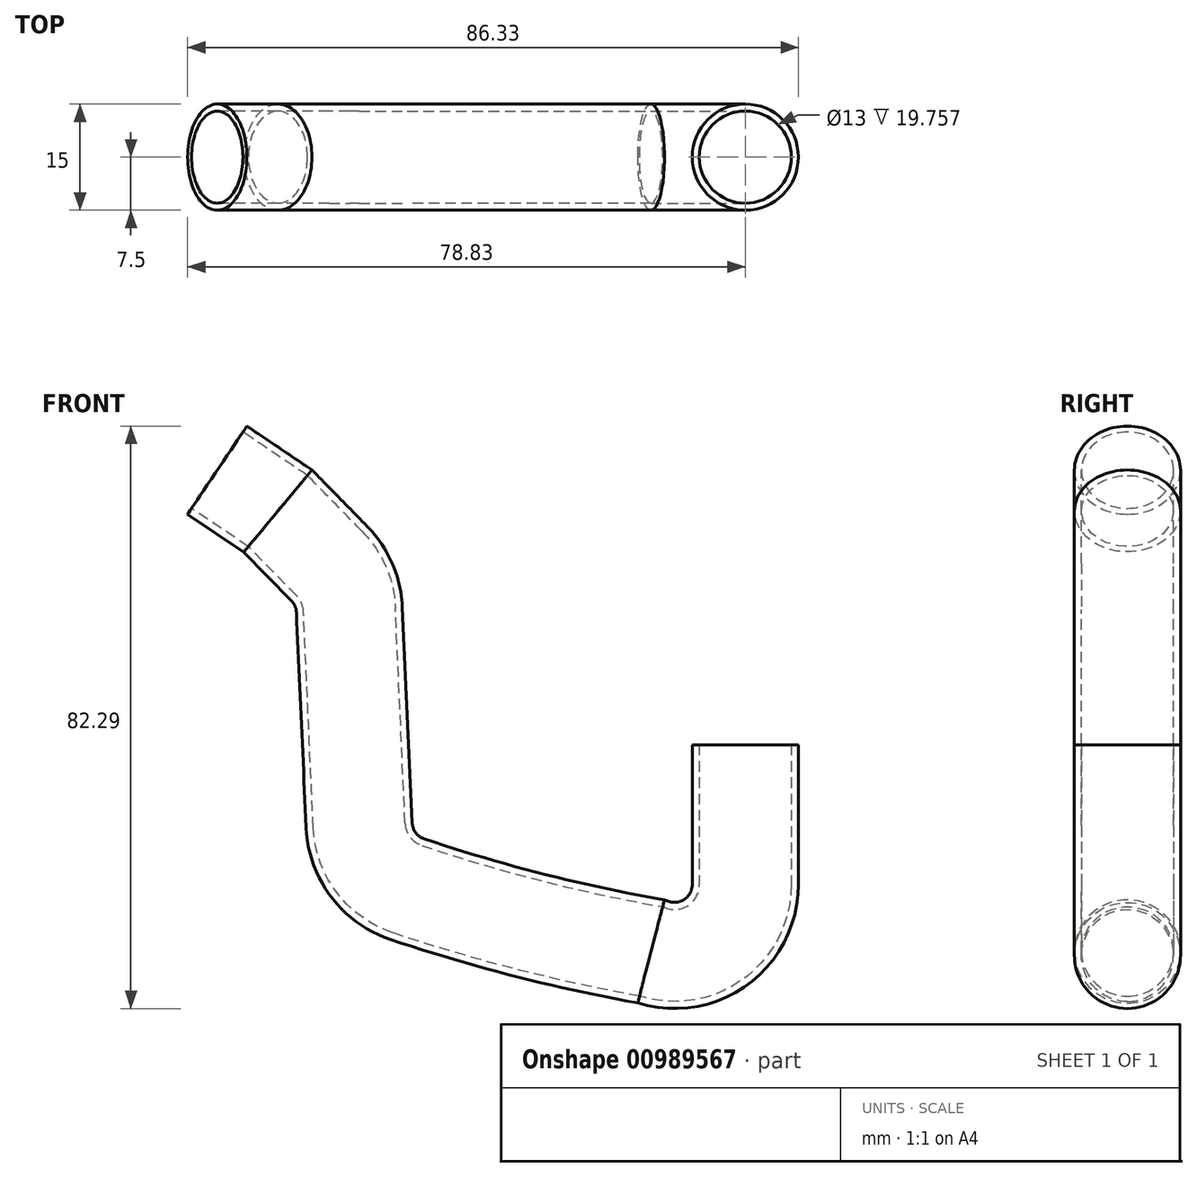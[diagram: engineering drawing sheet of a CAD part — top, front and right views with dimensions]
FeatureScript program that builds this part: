
annotation { "Feature Type Name" : "Feature", "Feature Type Description" : "" }
export const myFeature = defineFeature(function(context is Context, id is Id, definition is map)
    precondition{}
    {
        {
            var Q0;
            Q0=qCreatedBy(makeId("Top.planeOp"), FACE);
            var sketch = newSketch(context, id + "F0", { "sketchPlane" : qUnion([Q0])});
            skCircle(sketch, "E0", {"center": v(0, 0) * mm, "radius": 7.5 * mm});
            skCircle(sketch, "E1", {"center": v(0, 0) * mm, "radius": 6.5 * mm});
            skSolve(sketch);
        }
        {
            var Q0;
            Q0=qCreatedBy(makeId("Front.planeOp"), FACE);
            var sketch = newSketch(context, id + "F1", { "sketchPlane" : qUnion([Q0])});
            skLineSegment(sketch, "E2", {"start": v(0, 0) * mm, "end": v(0, -19.76) * mm});
            skArc(sketch, "E3.filletArc", {"start": v(-13.34, -29.18) * mm, "mid": v(-4.23, -27.92) * mm, "end": v(0, -19.76) * mm});
            skLineSegment(sketch, "E4", {"start": v(-66.07, 33.03) * mm, "end": v(-74.64, 38.8) * mm});
            skArc(sketch, "E5", {"start": v(-47.79, -20.39) * mm, "mid": v(-30.72, -25.43) * mm, "end": v(-13.34, -29.18) * mm});
            skLineSegment(sketch, "E6", {"start": v(-54.59, -11.36) * mm, "end": v(-55.96, 19.08) * mm});
            skLineSegment(sketch, "E7", {"start": v(-58.8, 25.63) * mm, "end": v(-66.07, 33.03) * mm});
            skPoint(sketch, "E8.visualSharp", {"position": v(-56.13, 22.9) * mm});
            skArc(sketch, "E8.filletArc", {"start": v(-55.96, 19.08) * mm, "mid": v(-56.78, 22.61) * mm, "end": v(-58.8, 25.63) * mm});
            skPoint(sketch, "E9.visualSharp", {"position": v(-54.28, -18.1) * mm});
            skArc(sketch, "E9.filletArc", {"start": v(-54.59, -11.36) * mm, "mid": v(-52.59, -16.92) * mm, "end": v(-47.79, -20.39) * mm});
            skSolve(sketch);
        }
        {
            var Q0;
            Q0 = qSketchRegion(id + "F0", true);
            var Q1;
            Q1 = qConstructionFilter(qBodyType(qCreatedBy(id + "F1" ,EDGE), BodyType.WIRE), ConstructionObject.NO);
            sweep(context, id + "F2", {"profiles" : qUnion([Q0]), "path" : qUnion([Q1])});
        }
    });
